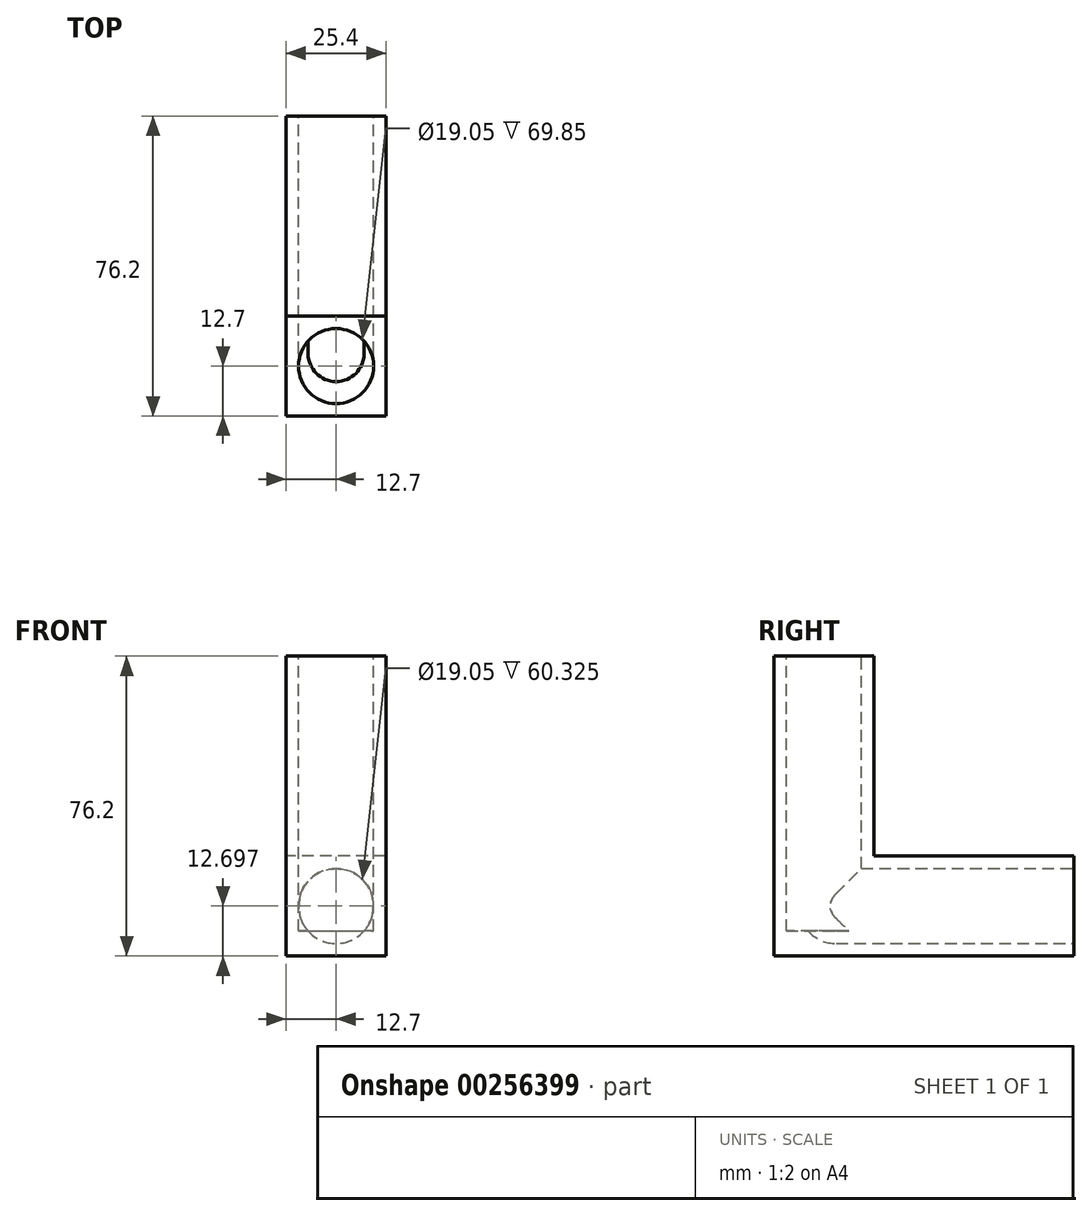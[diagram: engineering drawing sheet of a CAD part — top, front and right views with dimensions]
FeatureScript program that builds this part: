
annotation { "Feature Type Name" : "Feature", "Feature Type Description" : "" }
export const myFeature = defineFeature(function(context is Context, id is Id, definition is map)
    precondition{}
    {
        {
            var Q0;
            Q0=qCreatedBy(makeId("Front.planeOp"),FACE);
            var sketch = newSketch(context, id + "F0", { "sketchPlane" : qUnion([Q0])});
            skLineSegment(sketch, "E0.bottom", {"start": v(12.72, 11.37) * mm, "end": v(-12.68, 11.37) * mm});
            skLineSegment(sketch, "E0.top", {"start": v(12.72, -14.03) * mm, "end": v(-12.68, -14.03) * mm});
            skLineSegment(sketch, "E0.left", {"start": v(12.72, 11.37) * mm, "end": v(12.72, -14.03) * mm});
            skLineSegment(sketch, "E0.right", {"start": v(-12.68, 11.37) * mm, "end": v(-12.68, -14.03) * mm});
            skPoint(sketch, "E0.middle", {"position": v(0.02, -1.33) * mm});
            skSolve(sketch);
        }
        {
            var Q0;
            Q0=makeQuery(id+"F0.imprint","IMPRINT",FACE,{"disambiguationData":[TD([[makeQuery(id+"F0.imprint","IMPRINT",EDGE,{"derivedFrom":sQuery(id+"F0.wireOp",EDGE,"E0.bottom")}),1.0]])]});
            extrude(context, id + "F1", {"entities" : qUnion([Q0]), "depth" : 76.2 * mm});
        }
        {
            var Q0;
            Q0=makeQuery(id+"F1.opExtrude","SWEPT_FACE",FACE,{"disambiguationData":[OSD([sQuery(id+"F0.wireOp",EDGE,"E0.bottom")])]});
            var sketch = newSketch(context, id + "F2", { "sketchPlane" : qUnion([Q0])});
            skLineSegment(sketch, "E1.bottom", {"start": v(12.72, -76.2) * mm, "end": v(-12.68, -76.2) * mm});
            skLineSegment(sketch, "E1.top", {"start": v(12.72, -50.8) * mm, "end": v(-12.68, -50.8) * mm});
            skLineSegment(sketch, "E1.left", {"start": v(12.72, -76.2) * mm, "end": v(12.72, -50.8) * mm});
            skLineSegment(sketch, "E1.right", {"start": v(-12.68, -76.2) * mm, "end": v(-12.68, -50.8) * mm});
            skSolve(sketch);
        }
        {
            var Q0;
            Q0=makeQuery(id+"F2.imprint","IMPRINT",FACE,{"disambiguationData":[TD([[makeQuery(id+"F2.imprint","IMPRINT",EDGE,{"derivedFrom":sQuery(id+"F2.wireOp",EDGE,"E1.bottom")}),-1.0]])]});
            extrude(context, id + "F3", {"entities" : qUnion([Q0]), "operationType" : NewBodyOperationType.ADD, "depth" : 50.8 * mm});
        }
        {
            var Q0;
            Q0=makeQuery(id+"F1.opExtrude","CAP_FACE",FACE,{"disambiguationData":[OSD([sQuery(id+"F0.wireOp",EDGE,"E0.bottom"),sQuery(id+"F0.wireOp",EDGE,"E0.top"),sQuery(id+"F0.wireOp",EDGE,"E0.left"),sQuery(id+"F0.wireOp",EDGE,"E0.right")])],"isStart":true});
            var sketch = newSketch(context, id + "F4", { "sketchPlane" : qUnion([Q0])});
            skLineSegment(sketch, "E2", {"start": v(12.68, -1.33) * mm, "end": v(-12.72, -1.33) * mm});
            skLineSegment(sketch, "E3", {"start": v(-0.02, -14.03) * mm, "end": v(-0.02, -1.33) * mm});
            skCircle(sketch, "E4", {"center": v(-0.02, -1.33) * mm, "radius": 9.53 * mm});
            skSolve(sketch);
        }
        {
            var Q0;
            {var subQ0=sQuery(id+"F4.wireOp",EDGE,"E3");var subQ1=sQuery(id+"F4.wireOp",EDGE,"E2");var subQ2=makeQuery(id+"F4.imprint","INTERSECT",VERTEX,{"derivedFrom":[subQ1,subQ0]});Q0=makeQuery(id+"F4.imprint","IMPRINT",FACE,{"disambiguationData":[TD([[makeQuery(id+"F4.imprint","IMPRINT",EDGE,{"disambiguationData":[TD([[subQ2,1.0]])],"derivedFrom":subQ1}),1.0]])]});}
            var Q1;
            {var subQ0=sQuery(id+"F4.wireOp",EDGE,"E3");var subQ1=sQuery(id+"F4.wireOp",EDGE,"E2");var subQ2=makeQuery(id+"F4.imprint","INTERSECT",VERTEX,{"derivedFrom":[subQ1,subQ0]});Q1=makeQuery(id+"F4.imprint","IMPRINT",FACE,{"disambiguationData":[TD([[makeQuery(id+"F4.imprint","IMPRINT",EDGE,{"disambiguationData":[TD([[subQ2,-1.0]])],"derivedFrom":subQ1}),1.0]])]});}
            var Q2;
            {var subQ0=sQuery(id+"F4.wireOp",EDGE,"E2");var subQ1=makeQuery(id+"F4.imprint","INTERSECT",VERTEX,{"derivedFrom":[subQ0,sQuery(id+"F4.wireOp",EDGE,"E3")]});Q2=makeQuery(id+"F4.imprint","IMPRINT",FACE,{"disambiguationData":[TD([[makeQuery(id+"F4.imprint","IMPRINT",EDGE,{"disambiguationData":[TD([[subQ1,1.0]])],"derivedFrom":subQ0}),-1.0]])]});}
            extrude(context, id + "F5", {"entities" : qUnion([Q0, Q1, Q2]), "operationType" : NewBodyOperationType.REMOVE, "oppositeDirection" : true, "depth" : 69.85 * mm});
        }
        {
            var Q0;
            Q0=makeQuery(id+"F3.opExtrude","CAP_FACE",FACE,{"disambiguationData":[OSD([sQuery(id+"F2.wireOp",EDGE,"E1.bottom"),sQuery(id+"F2.wireOp",EDGE,"E1.top"),sQuery(id+"F2.wireOp",EDGE,"E1.left"),sQuery(id+"F2.wireOp",EDGE,"E1.right")])],"isStart":false});
            var sketch = newSketch(context, id + "F6", { "sketchPlane" : qUnion([Q0])});
            skLineSegment(sketch, "E5", {"start": v(0.02, -50.8) * mm, "end": v(0.02, -76.2) * mm});
            skLineSegment(sketch, "E6", {"start": v(-12.68, -63.5) * mm, "end": v(0.02, -63.5) * mm});
            skCircle(sketch, "E7", {"center": v(0.02, -63.5) * mm, "radius": 9.53 * mm});
            skSolve(sketch);
        }
        {
            var Q0;
            Q0=makeQuery(id+"F5.boolean.opBoolean","COPY",EDGE,{"derivedFrom":makeQuery(id+"F5.opExtrude","CAP_EDGE",EDGE,{"disambiguationData":[OSD([sQuery(id+"F4.wireOp",EDGE,"E4")])],"isStart":false})});
            fillet(context, id + "F7", {"entities" : qUnion([Q0]), "radius" : 9.52 * mm, "tangentPropagation" : true, "allowEdgeOverflow" : false});
        }
        {
            var Q0;
            {var subQ0=sQuery(id+"F6.wireOp",EDGE,"E5");var subQ1=makeQuery(id+"F6.imprint","INTERSECT",VERTEX,{"derivedFrom":[subQ0,sQuery(id+"F6.wireOp",EDGE,"E6")]});Q0=makeQuery(id+"F6.imprint","IMPRINT",FACE,{"disambiguationData":[TD([[makeQuery(id+"F6.imprint","IMPRINT",EDGE,{"disambiguationData":[TD([[subQ1,1.0]])],"derivedFrom":subQ0}),1.0]])]});}
            var Q1;
            {var subQ0=sQuery(id+"F6.wireOp",EDGE,"E6");var subQ1=sQuery(id+"F6.wireOp",EDGE,"E5");var subQ2=makeQuery(id+"F6.imprint","INTERSECT",VERTEX,{"derivedFrom":[subQ1,subQ0]});Q1=makeQuery(id+"F6.imprint","IMPRINT",FACE,{"disambiguationData":[TD([[makeQuery(id+"F6.imprint","IMPRINT",EDGE,{"disambiguationData":[TD([[subQ2,-1.0]])],"derivedFrom":subQ1}),-1.0]])]});}
            var Q2;
            {var subQ0=sQuery(id+"F6.wireOp",EDGE,"E6");var subQ1=sQuery(id+"F6.wireOp",EDGE,"E5");var subQ2=makeQuery(id+"F6.imprint","INTERSECT",VERTEX,{"derivedFrom":[subQ1,subQ0]});Q2=makeQuery(id+"F6.imprint","IMPRINT",FACE,{"disambiguationData":[TD([[makeQuery(id+"F6.imprint","IMPRINT",EDGE,{"disambiguationData":[TD([[subQ2,1.0]])],"derivedFrom":subQ1}),-1.0]])]});}
            extrude(context, id + "F8", {"entities" : qUnion([Q0, Q1, Q2]), "operationType" : NewBodyOperationType.REMOVE, "oppositeDirection" : true, "depth" : 69.85 * mm});
        }
    });
